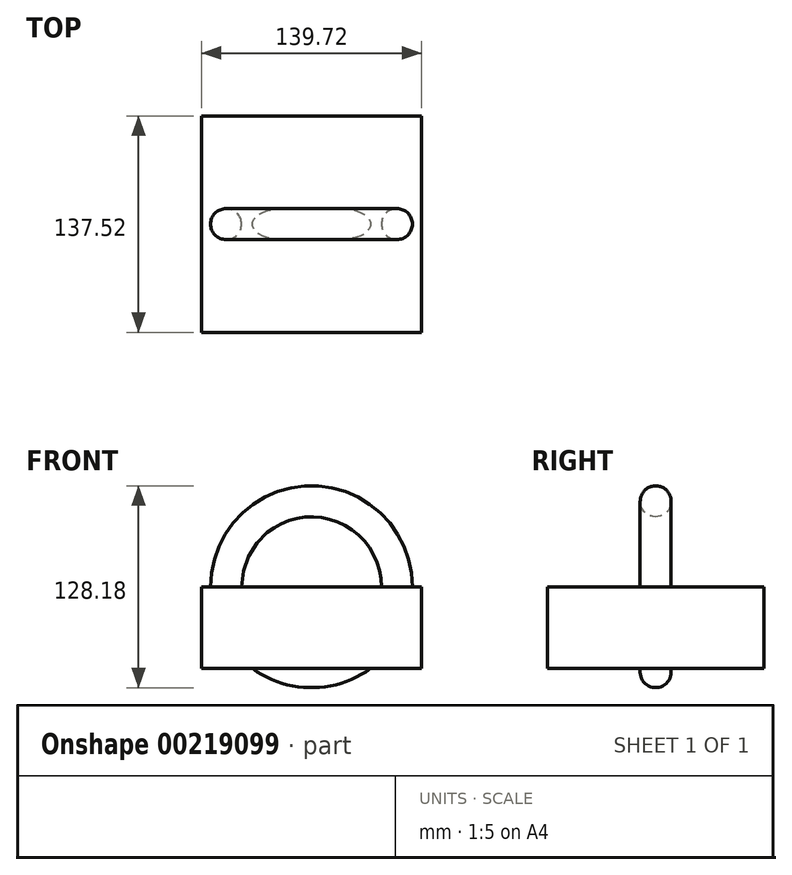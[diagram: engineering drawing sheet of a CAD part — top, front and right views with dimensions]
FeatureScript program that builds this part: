
annotation { "Feature Type Name" : "Feature", "Feature Type Description" : "" }
export const myFeature = defineFeature(function(context is Context, id is Id, definition is map)
    precondition{}
    {
        {
            var Q0;
            Q0=qCreatedBy(makeId("Top.planeOp"),FACE);
            var sketch = newSketch(context, id + "F0", { "sketchPlane" : qUnion([Q0])});
            skLineSegment(sketch, "E0.bottom", {"start": v(69.86, -68.76) * mm, "end": v(-69.86, -68.76) * mm});
            skLineSegment(sketch, "E0.top", {"start": v(69.86, 68.76) * mm, "end": v(-69.86, 68.76) * mm});
            skLineSegment(sketch, "E0.left", {"start": v(69.86, -68.76) * mm, "end": v(69.86, 68.76) * mm});
            skLineSegment(sketch, "E0.right", {"start": v(-69.86, -68.76) * mm, "end": v(-69.86, 68.76) * mm});
            skPoint(sketch, "E0.middle", {"position": v(0, 0) * mm});
            skLineSegment(sketch, "E1", {"start": v(0, 68.76) * mm, "end": v(0, -68.76) * mm});
            skSolve(sketch);
        }
        {
            var Q0;
            Q0=qCreatedBy(makeId("Top.planeOp"),FACE);
            var sketch = newSketch(context, id + "F1", { "sketchPlane" : qUnion([Q0])});
            skCircle(sketch, "E2", {"center": v(54.26, 0) * mm, "radius": 9.82 * mm});
            skSolve(sketch);
        }
        {
            var Q0;
            {var subQ0=sQuery(id+"F0.wireOp",EDGE,"E0.right");Q0=makeQuery(id+"F0.imprint","IMPRINT",FACE,{"disambiguationData":[TD([[makeQuery(id+"F0.imprint","IMPRINT",EDGE,{"derivedFrom":subQ0}),-1.0]])]});}
            var Q1;
            {var subQ0=sQuery(id+"F0.wireOp",EDGE,"E0.left");Q1=makeQuery(id+"F0.imprint","IMPRINT",FACE,{"disambiguationData":[TD([[makeQuery(id+"F0.imprint","IMPRINT",EDGE,{"derivedFrom":subQ0}),1.0]])]});}
            extrude(context, id + "F2", {"entities" : qUnion([Q0, Q1]), "oppositeDirection" : true, "depth" : 52 * mm});
        }
        {
            var Q0;
            Q0=makeQuery(id+"F1.imprint","IMPRINT",FACE,{"disambiguationData":[TD([[makeQuery(id+"F1.imprint","IMPRINT",EDGE,{"derivedFrom":sQuery(id+"F1.wireOp",EDGE,"E2")}),1.0]])]});
            var Q1;
            Q1=sQuery(id+"F0.wireOp",EDGE,"E1");
            revolve(context, id + "F3", {"operationType" : NewBodyOperationType.ADD, "entities" : qUnion([Q0]), "axis" : qUnion([Q1]), "revolveType" : RevolveType.FULL});
        }
    });
